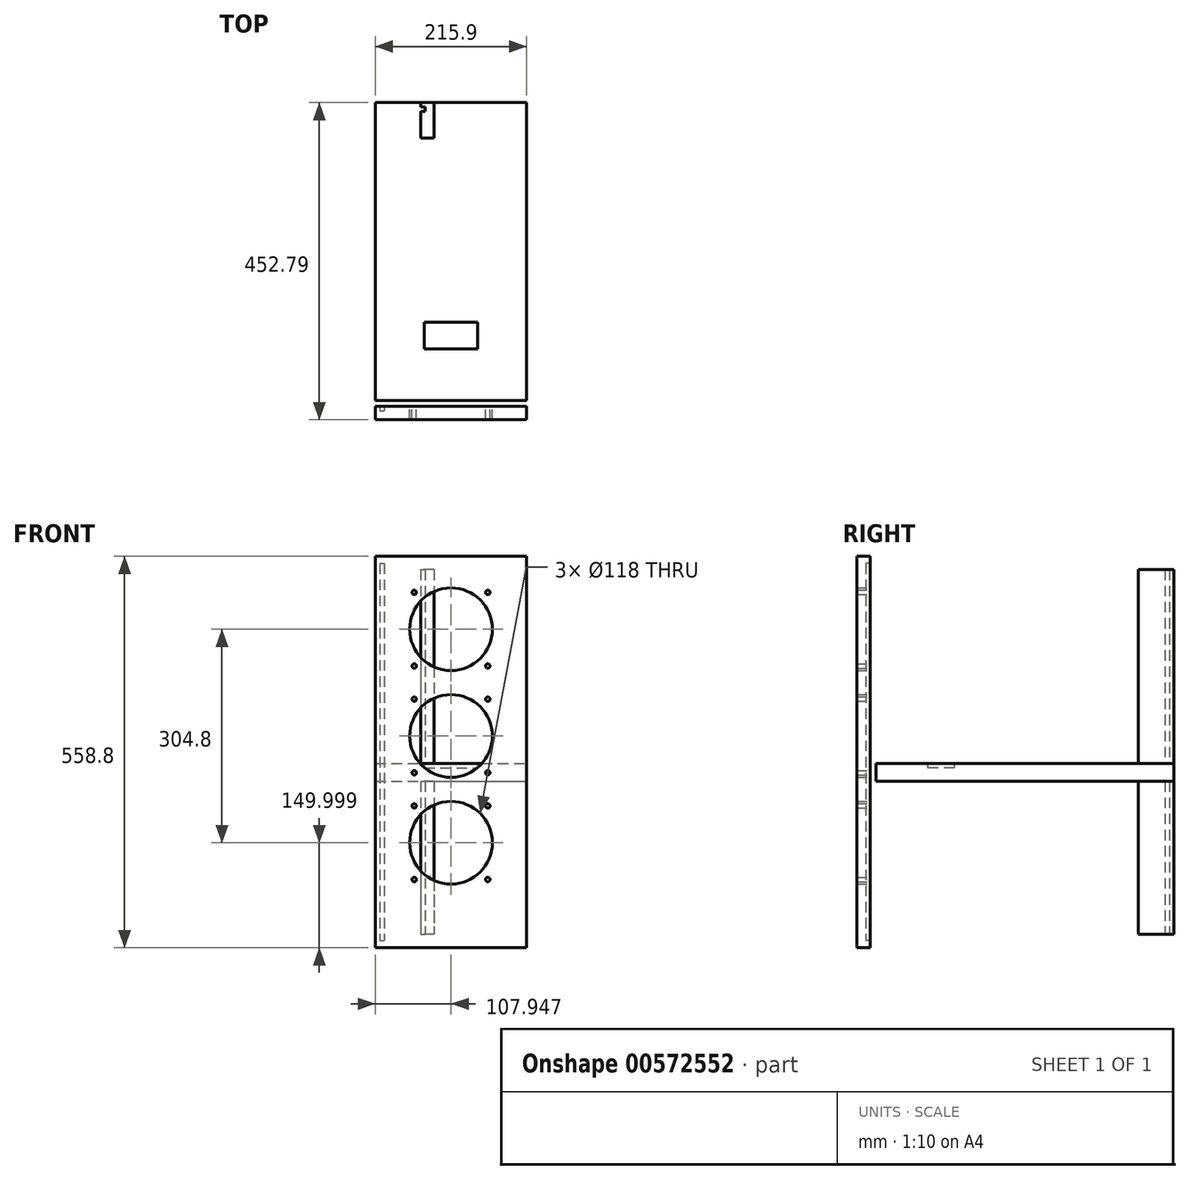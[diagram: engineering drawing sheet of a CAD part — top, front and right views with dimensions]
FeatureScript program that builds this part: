
annotation { "Feature Type Name" : "Feature", "Feature Type Description" : "" }
export const myFeature = defineFeature(function(context is Context, id is Id, definition is map)
    precondition{}
    {
        {
            var Q0;
            Q0=qCreatedBy(makeId("Front.planeOp"),FACE);
            var sketch = newSketch(context, id + "F0", { "sketchPlane" : qUnion([Q0])});
            skLineSegment(sketch, "E0.bottom", {"start": v(-71.32, 308.63) * mm, "end": v(144.58, 308.63) * mm});
            skLineSegment(sketch, "E0.top", {"start": v(-71.32, -250.17) * mm, "end": v(144.58, -250.17) * mm});
            skLineSegment(sketch, "E0.left", {"start": v(-71.32, 308.63) * mm, "end": v(-71.32, -250.17) * mm});
            skLineSegment(sketch, "E0.right", {"start": v(144.58, 308.63) * mm, "end": v(144.58, -250.17) * mm});
            skLineSegment(sketch, "E1.bottom", {"start": v(-64.97, 298.47) * mm, "end": v(-58.57, 298.47) * mm});
            skLineSegment(sketch, "E1.top", {"start": v(-64.97, -240.01) * mm, "end": v(-58.57, -240.01) * mm});
            skLineSegment(sketch, "E1.left", {"start": v(-64.97, 298.47) * mm, "end": v(-64.97, -240.01) * mm});
            skLineSegment(sketch, "E1.right", {"start": v(-58.57, 298.47) * mm, "end": v(-58.57, -240.01) * mm});
            skCircle(sketch, "E2", {"center": v(36.63, -100.17) * mm, "radius": 59 * mm});
            skCircle(sketch, "E3", {"center": v(36.63, 52.23) * mm, "radius": 59 * mm});
            skCircle(sketch, "E4", {"center": v(36.63, 204.63) * mm, "radius": 59 * mm});
            skCircle(sketch, "E5", {"center": v(-15.87, 257.13) * mm, "radius": 3.18 * mm});
            skCircle(sketch, "E6", {"center": v(89.13, 257.13) * mm, "radius": 3.18 * mm});
            skCircle(sketch, "E7", {"center": v(89.13, 152.13) * mm, "radius": 3.18 * mm});
            skCircle(sketch, "E8", {"center": v(-15.87, 152.13) * mm, "radius": 3.18 * mm});
            skCircle(sketch, "E9", {"center": v(-15.87, 104.73) * mm, "radius": 3.18 * mm});
            skCircle(sketch, "E10", {"center": v(89.13, 104.73) * mm, "radius": 3.18 * mm});
            skCircle(sketch, "E11", {"center": v(89.13, -47.67) * mm, "radius": 3.18 * mm});
            skCircle(sketch, "E12", {"center": v(-15.87, -47.67) * mm, "radius": 3.18 * mm});
            skCircle(sketch, "E13", {"center": v(-15.87, -152.67) * mm, "radius": 3.18 * mm});
            skCircle(sketch, "E14", {"center": v(89.13, -152.67) * mm, "radius": 3.18 * mm});
            skCircle(sketch, "E15", {"center": v(-15.87, -0.27) * mm, "radius": 3.18 * mm});
            skCircle(sketch, "E16", {"center": v(89.13, -0.27) * mm, "radius": 3.18 * mm});
            skSolve(sketch);
        }
        {
            var Q0;
            Q0=makeQuery(id+"F0.imprint","IMPRINT",FACE,{"disambiguationData":[TD([[makeQuery(id+"F0.imprint","IMPRINT",EDGE,{"derivedFrom":sQuery(id+"F0.wireOp",EDGE,"E0.bottom")}),-1.0]])]});
            var Q1;
            Q1=makeQuery(id+"F0.imprint","IMPRINT",FACE,{"disambiguationData":[TD([[makeQuery(id+"F0.imprint","IMPRINT",EDGE,{"derivedFrom":sQuery(id+"F0.wireOp",EDGE,"E1.bottom")}),-1.0]])]});
            extrude(context, id + "F1", {"entities" : qUnion([Q0, Q1]), "depth" : 12.7 * mm, "offsetDistance" : 25.4 * mm});
        }
        {
            var Q0;
            Q0=makeQuery(id+"F0.imprint","IMPRINT",FACE,{"disambiguationData":[TD([[makeQuery(id+"F0.imprint","IMPRINT",EDGE,{"derivedFrom":sQuery(id+"F0.wireOp",EDGE,"E0.bottom")}),-1.0]])]});
            extrude(context, id + "F2", {"entities" : qUnion([Q0]), "operationType" : NewBodyOperationType.ADD, "oppositeDirection" : true, "depth" : 6.35 * mm, "offsetDistance" : 25.4 * mm});
        }
        {
            var Q0;
            Q0=qCreatedBy(makeId("Top.planeOp"),FACE);
            var sketch = newSketch(context, id + "F3", { "sketchPlane" : qUnion([Q0])});
            skPoint(sketch, "E17.0", {"position": v(-71.32, 6.35) * mm});
            skPoint(sketch, "E17.1", {"position": v(144.58, 6.35) * mm});
            skLineSegment(sketch, "E18.bottom", {"start": v(-71.32, 14.64) * mm, "end": v(144.58, 14.64) * mm});
            skLineSegment(sketch, "E18.top", {"start": v(-71.32, 440.1) * mm, "end": v(144.58, 440.1) * mm});
            skLineSegment(sketch, "E18.left", {"start": v(-71.32, 14.64) * mm, "end": v(-71.32, 440.1) * mm});
            skLineSegment(sketch, "E18.right", {"start": v(144.58, 14.64) * mm, "end": v(144.58, 440.1) * mm});
            skPoint(sketch, "E19.0", {"position": v(-64.97, 6.35) * mm});
            skPoint(sketch, "E19.1", {"position": v(-58.57, 6.35) * mm});
            skLineSegment(sketch, "E20.bottom", {"start": v(-64.97, 11.3) * mm, "end": v(-58.57, 11.3) * mm});
            skLineSegment(sketch, "E20.top", {"start": v(-64.97, 449.45) * mm, "end": v(-58.57, 449.45) * mm});
            skLineSegment(sketch, "E20.left", {"start": v(-64.97, 11.3) * mm, "end": v(-64.97, 449.45) * mm});
            skLineSegment(sketch, "E20.right", {"start": v(-58.57, 11.3) * mm, "end": v(-58.57, 449.45) * mm});
            skLineSegment(sketch, "E21.bottom", {"start": v(-1.47, 126.7) * mm, "end": v(74.73, 126.7) * mm});
            skLineSegment(sketch, "E21.top", {"start": v(-1.47, 88.6) * mm, "end": v(74.73, 88.6) * mm});
            skLineSegment(sketch, "E21.left", {"start": v(-1.47, 126.7) * mm, "end": v(-1.47, 88.6) * mm});
            skLineSegment(sketch, "E21.right", {"start": v(74.73, 126.7) * mm, "end": v(74.73, 88.6) * mm});
            skLineSegment(sketch, "E22.bottom", {"start": v(-59.9, 433.74) * mm, "end": v(134.42, 433.74) * mm});
            skLineSegment(sketch, "E22.top", {"start": v(-59.9, 427.4) * mm, "end": v(134.42, 427.4) * mm});
            skLineSegment(sketch, "E22.left", {"start": v(-59.9, 433.74) * mm, "end": v(-59.9, 427.4) * mm});
            skLineSegment(sketch, "E22.right", {"start": v(134.42, 433.74) * mm, "end": v(134.42, 427.4) * mm});
            skSolve(sketch);
        }
        {
            var Q0;
            {var subQ0=sQuery(id+"F3.wireOp",EDGE,"E18.left");Q0=makeQuery(id+"F3.imprint","IMPRINT",FACE,{"disambiguationData":[TD([[makeQuery(id+"F3.imprint","IMPRINT",EDGE,{"derivedFrom":subQ0}),-1.0]])]});}
            var Q1;
            {var subQ7=sQuery(id+"F3.wireOp",EDGE,"E22.left");Q1=makeQuery(id+"F3.imprint","IMPRINT",FACE,{"disambiguationData":[TD([[makeQuery(id+"F3.imprint","IMPRINT",EDGE,{"derivedFrom":subQ7}),-1.0]])]});}
            var Q2;
            {var subQ0=sQuery(id+"F3.wireOp",EDGE,"E18.right");var subQ1=sQuery(id+"F3.wireOp",EDGE,"E18.top");var subQ2=makeQuery(id+"F3.imprint","INTERSECT",VERTEX,{"derivedFrom":[subQ1,subQ0]});Q2=makeQuery(id+"F3.imprint","IMPRINT",FACE,{"disambiguationData":[TD([[makeQuery(id+"F3.imprint","IMPRINT",EDGE,{"disambiguationData":[TD([[subQ2,1.0]])],"derivedFrom":subQ1}),-1.0]])]});}
            var Q3;
            {var subQ5=sQuery(id+"F3.wireOp",EDGE,"E22.left");Q3=makeQuery(id+"F3.imprint","IMPRINT",FACE,{"disambiguationData":[TD([[makeQuery(id+"F3.imprint","IMPRINT",EDGE,{"derivedFrom":subQ5}),1.0]])]});}
            var Q4;
            Q4=makeQuery(id+"F3.imprint","IMPRINT",FACE,{"disambiguationData":[TD([[makeQuery(id+"F3.imprint","IMPRINT",EDGE,{"derivedFrom":sQuery(id+"F3.wireOp",EDGE,"E21.bottom")}),1.0]])]});
            var Q5;
            {var subQ5=sQuery(id+"F3.wireOp",EDGE,"E22.right");Q5=makeQuery(id+"F3.imprint","IMPRINT",FACE,{"disambiguationData":[TD([[makeQuery(id+"F3.imprint","IMPRINT",EDGE,{"derivedFrom":subQ5}),-1.0]])]});}
            extrude(context, id + "F4", {"entities" : qUnion([Q0, Q1, Q2, Q3, Q4, Q5]), "depth" : 12.7 * mm, "offsetDistance" : 25.4 * mm});
        }
        {
            var Q0;
            {var subQ0=sQuery(id+"F3.wireOp",EDGE,"E18.right");var subQ1=sQuery(id+"F3.wireOp",EDGE,"E18.top");var subQ2=makeQuery(id+"F3.imprint","INTERSECT",VERTEX,{"derivedFrom":[subQ1,subQ0]});Q0=makeQuery(id+"F3.imprint","IMPRINT",FACE,{"disambiguationData":[TD([[makeQuery(id+"F3.imprint","IMPRINT",EDGE,{"disambiguationData":[TD([[subQ2,1.0]])],"derivedFrom":subQ1}),-1.0]])]});}
            var Q1;
            Q1=makeQuery(id+"F3.imprint","IMPRINT",FACE,{"disambiguationData":[TD([[makeQuery(id+"F3.imprint","IMPRINT",EDGE,{"derivedFrom":sQuery(id+"F3.wireOp",EDGE,"E21.bottom")}),1.0]])]});
            var Q2;
            {var subQ0=sQuery(id+"F3.wireOp",EDGE,"E18.left");Q2=makeQuery(id+"F3.imprint","IMPRINT",FACE,{"disambiguationData":[TD([[makeQuery(id+"F3.imprint","IMPRINT",EDGE,{"derivedFrom":subQ0}),-1.0]])]});}
            extrude(context, id + "F5", {"entities" : qUnion([Q0, Q1, Q2]), "operationType" : NewBodyOperationType.ADD, "oppositeDirection" : true, "depth" : 6.35 * mm, "offsetDistance" : 25.4 * mm});
        }
        {
            var Q0;
            Q0=qCreatedBy(makeId("Top.planeOp"),FACE);
            var sketch = newSketch(context, id + "F6", { "sketchPlane" : qUnion([Q0])});
            skPoint(sketch, "E23.0", {"position": v(144.58, 440.1) * mm});
            skPoint(sketch, "E23.1", {"position": v(144.58, 14.64) * mm});
            skPoint(sketch, "E23.2", {"position": v(-71.32, 14.64) * mm});
            skPoint(sketch, "E23.3", {"position": v(-71.32, 440.1) * mm});
            skPoint(sketch, "E23.4", {"position": v(-64.97, 440.1) * mm});
            skPoint(sketch, "E23.5", {"position": v(-58.57, 440.1) * mm});
            skLineSegment(sketch, "E24.bottom", {"start": v(-71.32, 14.64) * mm, "end": v(144.58, 14.64) * mm});
            skLineSegment(sketch, "E24.top", {"start": v(-71.32, 440.1) * mm, "end": v(144.58, 440.1) * mm});
            skLineSegment(sketch, "E24.left", {"start": v(-71.32, 14.64) * mm, "end": v(-71.32, 440.1) * mm});
            skLineSegment(sketch, "E24.right", {"start": v(144.58, 14.64) * mm, "end": v(144.58, 440.1) * mm});
            skLineSegment(sketch, "E25.bottom", {"start": v(-58.57, 447.35) * mm, "end": v(-64.97, 447.35) * mm});
            skLineSegment(sketch, "E25.top", {"start": v(-58.57, 9.2) * mm, "end": v(-64.97, 9.2) * mm});
            skLineSegment(sketch, "E25.left", {"start": v(-58.57, 447.35) * mm, "end": v(-58.57, 9.2) * mm});
            skLineSegment(sketch, "E25.right", {"start": v(-64.97, 447.35) * mm, "end": v(-64.97, 9.2) * mm});
            skLineSegment(sketch, "E26.bottom", {"start": v(-58.57, 433.74) * mm, "end": v(131.88, 433.74) * mm});
            skLineSegment(sketch, "E26.top", {"start": v(-58.57, 427.4) * mm, "end": v(131.88, 427.4) * mm});
            skLineSegment(sketch, "E26.left", {"start": v(-58.57, 433.74) * mm, "end": v(-58.57, 427.4) * mm});
            skLineSegment(sketch, "E26.right", {"start": v(131.88, 433.74) * mm, "end": v(131.88, 427.4) * mm});
            skSolve(sketch);
        }
        {
            var Q0;
            {var subQ0=sQuery(id+"F6.wireOp",EDGE,"E24.left");Q0=makeQuery(id+"F6.imprint","IMPRINT",FACE,{"disambiguationData":[TD([[makeQuery(id+"F6.imprint","IMPRINT",EDGE,{"derivedFrom":subQ0}),-1.0]])]});}
            var Q1;
            {var subQ0=sQuery(id+"F6.wireOp",EDGE,"E25.right");var subQ1=sQuery(id+"F6.wireOp",EDGE,"E24.bottom");var subQ2=makeQuery(id+"F6.imprint","INTERSECT",VERTEX,{"derivedFrom":[subQ1,subQ0]});Q1=makeQuery(id+"F6.imprint","IMPRINT",FACE,{"disambiguationData":[TD([[makeQuery(id+"F6.imprint","IMPRINT",EDGE,{"disambiguationData":[TD([[subQ2,-1.0]])],"derivedFrom":subQ1}),1.0]])]});}
            var Q2;
            {var subQ0=sQuery(id+"F6.wireOp",EDGE,"E24.right");Q2=makeQuery(id+"F6.imprint","IMPRINT",FACE,{"disambiguationData":[TD([[makeQuery(id+"F6.imprint","IMPRINT",EDGE,{"derivedFrom":subQ0}),1.0]])]});}
            var Q3;
            Q3=makeQuery(id+"F6.imprint","IMPRINT",FACE,{"disambiguationData":[TD([[makeQuery(id+"F6.imprint","IMPRINT",EDGE,{"derivedFrom":sQuery(id+"F6.wireOp",EDGE,"E26.bottom")}),-1.0]])]});
            extrude(context, id + "F7", {"entities" : qUnion([Q0, Q1, Q2, Q3]), "oppositeDirection" : true, "depth" : 12.7 * mm, "offsetDistance" : 25.4 * mm});
        }
        {
            var Q0;
            {var subQ0=sQuery(id+"F6.wireOp",EDGE,"E24.right");var subQ1=sQuery(id+"F6.wireOp",EDGE,"E24.bottom");var subQ2=makeQuery(id+"F6.imprint","INTERSECT",VERTEX,{"derivedFrom":[subQ1,subQ0]});Q0=makeQuery(id+"F6.imprint","IMPRINT",FACE,{"disambiguationData":[TD([[makeQuery(id+"F6.imprint","IMPRINT",EDGE,{"disambiguationData":[TD([[subQ2,1.0]])],"derivedFrom":subQ1}),1.0]])]});}
            var Q1;
            {var subQ0=sQuery(id+"F6.wireOp",EDGE,"E24.right");var subQ1=sQuery(id+"F6.wireOp",EDGE,"E24.top");var subQ2=makeQuery(id+"F6.imprint","INTERSECT",VERTEX,{"derivedFrom":[subQ1,subQ0]});Q1=makeQuery(id+"F6.imprint","IMPRINT",FACE,{"disambiguationData":[TD([[makeQuery(id+"F6.imprint","IMPRINT",EDGE,{"disambiguationData":[TD([[subQ2,1.0]])],"derivedFrom":subQ1}),-1.0]])]});}
            var Q2;
            {var subQ0=sQuery(id+"F6.wireOp",EDGE,"E24.left");Q2=makeQuery(id+"F6.imprint","IMPRINT",FACE,{"disambiguationData":[TD([[makeQuery(id+"F6.imprint","IMPRINT",EDGE,{"derivedFrom":subQ0}),-1.0]])]});}
            extrude(context, id + "F8", {"entities" : qUnion([Q0, Q1, Q2]), "operationType" : NewBodyOperationType.ADD, "depth" : 6.35 * mm, "offsetDistance" : 25.4 * mm});
        }
        {
            var Q0;
            Q0=qCreatedBy(makeId("Right.planeOp"),FACE);
            var sketch = newSketch(context, id + "F9", { "sketchPlane" : qUnion([Q0])});
            skPoint(sketch, "E27.0", {"position": v(6.35, 308.63) * mm});
            skPoint(sketch, "E27.1", {"position": v(6.35, -250.17) * mm});
            skPoint(sketch, "E27.2", {"position": v(440.1, 12.7) * mm});
            skLineSegment(sketch, "E28.bottom", {"start": v(440.1, 289.58) * mm, "end": v(389.3, 289.58) * mm});
            skLineSegment(sketch, "E28.top", {"start": v(440.1, -231.12) * mm, "end": v(389.3, -231.12) * mm});
            skLineSegment(sketch, "E28.left", {"start": v(440.1, 289.58) * mm, "end": v(440.1, -231.12) * mm});
            skLineSegment(sketch, "E28.right", {"start": v(389.3, 289.58) * mm, "end": v(389.3, -231.12) * mm});
            skLineSegment(sketch, "E29.bottom", {"start": v(427.4, 304.97) * mm, "end": v(433.74, 304.97) * mm});
            skLineSegment(sketch, "E29.top", {"start": v(427.4, -255.93) * mm, "end": v(433.74, -255.93) * mm});
            skLineSegment(sketch, "E29.left", {"start": v(427.4, 304.97) * mm, "end": v(427.4, -255.93) * mm});
            skLineSegment(sketch, "E29.right", {"start": v(433.74, 304.97) * mm, "end": v(433.74, -255.93) * mm});
            skSolve(sketch);
        }
        {
            var Q0;
            Q0=makeQuery(id+"F9.imprint","IMPRINT",FACE,{"disambiguationData":[TD([[makeQuery(id+"F9.imprint","IMPRINT",EDGE,{"derivedFrom":sQuery(id+"F9.wireOp",EDGE,"E28.bottom")}),1.0]])]});
            extrude(context, id + "F10", {"entities" : qUnion([Q0]), "depth" : 12.7 * mm, "offsetDistance" : 25.4 * mm});
        }
        {
            var Q0;
            {var subQ0=sQuery(id+"F9.wireOp",EDGE,"E28.left");Q0=makeQuery(id+"F9.imprint","IMPRINT",FACE,{"disambiguationData":[TD([[makeQuery(id+"F9.imprint","IMPRINT",EDGE,{"derivedFrom":subQ0}),-1.0]])]});}
            var Q1;
            {var subQ0=sQuery(id+"F9.wireOp",EDGE,"E28.right");Q1=makeQuery(id+"F9.imprint","IMPRINT",FACE,{"disambiguationData":[TD([[makeQuery(id+"F9.imprint","IMPRINT",EDGE,{"derivedFrom":subQ0}),1.0]])]});}
            extrude(context, id + "F11", {"entities" : qUnion([Q0, Q1]), "operationType" : NewBodyOperationType.ADD, "oppositeDirection" : true, "depth" : 6.35 * mm, "offsetDistance" : 25.4 * mm});
        }
    });
